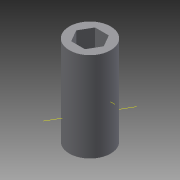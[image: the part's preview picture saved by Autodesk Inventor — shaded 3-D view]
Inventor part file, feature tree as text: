
AUTODESK INVENTOR PART (.ipt)
format: ipt  version: 2015 SP1 (Build 190203100, 203)  size: 116,224 bytes
history: native  units: mm
features: other x4, extrude x2, sketch x2, pattern_circular x1
ambient origin geometry x8: Origin, YZ Plane, XZ Plane, XY Plane, X Axis, Y Axis, Z Axis, Center Point
bodies: Body1 (feature_tree)
feature tree (9):
  other  "Sólido1"
  extrude  "Extrusión1"  Depth=12.0mm
  extrude  "Extrusión2"  Depth=6.0mm TaperAngle=0.0deg
  other  "Eje de trabajo1"
  other  "Eje de trabajo2"
  pattern_circular  "Patrón circular3"  Count=2 Angle=360.0deg
  sketch  "Boceto1"  dims[d0=8.0mm d1=12.0mm]
  sketch  "Boceto2"  dims[d2=7.0mm d3=0.0mm d4=6.0mm d5=0.0mm d19=20.0mm d20=360.0deg]
  other  "Punto de trabajo1"
